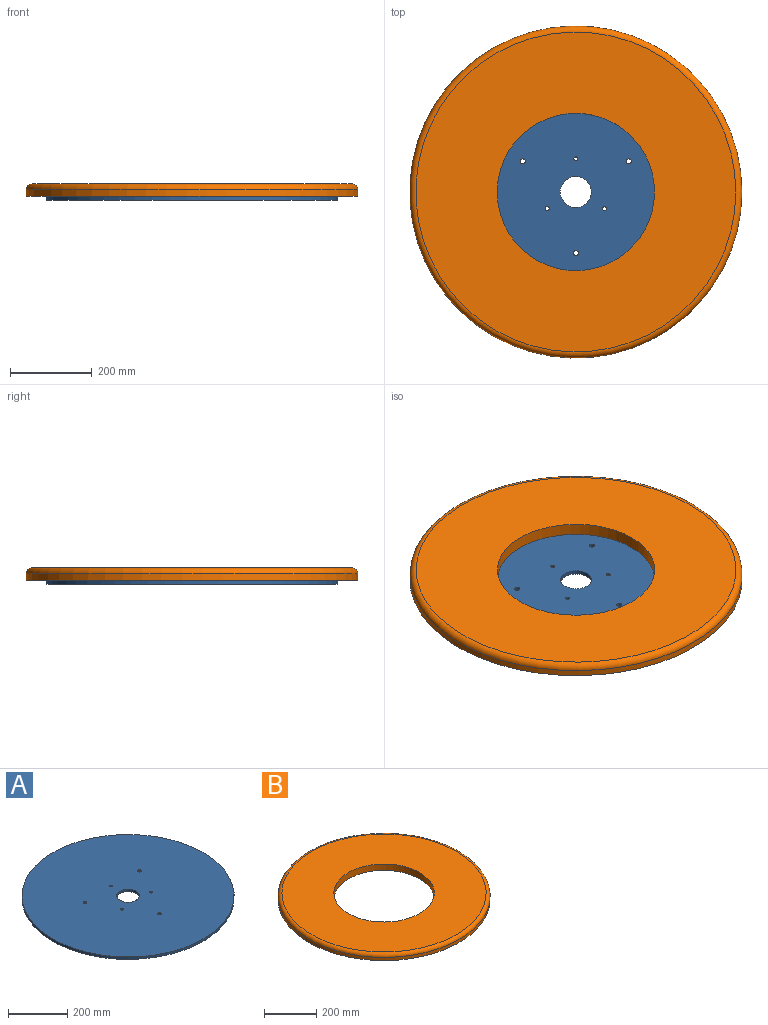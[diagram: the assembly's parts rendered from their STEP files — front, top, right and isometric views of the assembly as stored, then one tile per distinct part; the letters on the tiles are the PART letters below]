
ASSEMBLY  parts=2 mates=1
PART A: 10 faces, bbox 715x715x10 mm
  f0: cylinder r=357.5mm len=715mm, axis (0,0,-1), area 22462.4mm2, adj f1,f2
  f1: plane 715x715mm, normal (0,0,1), area 396315.1mm2, adj f0,f3,f4,f5,f6,f7,f8,f9
  f2: plane 715x715mm, normal (0,0,-1), area 396315.1mm2, adj f0,f3,f4,f5,f6,f7,f8,f9
  f3: cylinder r=38.25mm len=76.5mm, axis (0,0,-1), area 2403.3mm2, adj f1,f2
  f4: cylinder r=6.25mm len=12.5mm, axis (0,0,1), area 392.7mm2, adj f1,f2
  f5: cylinder r=6.25mm len=12.5mm, axis (0,0,1), area 392.7mm2, adj f1,f2
  f6: cylinder r=6.25mm len=12.5mm, axis (0,0,1), area 392.7mm2, adj f1,f2
  f7: cylinder r=5mm len=10mm, axis (0,0,1), area 314.2mm2, adj f1,f2
  f8: cylinder r=5mm len=10mm, axis (0,0,1), area 314.2mm2, adj f1,f2
  f9: cylinder r=5mm len=10mm, axis (0,0,1), area 314.2mm2, adj f1,f2
PART B: 5 faces, bbox 882.1x882.1x30 mm
  f0: cylinder r=407.5mm len=815mm, axis (0,0,-1), area 38406mm2, adj f2,f4
  f1: plane 785x785mm, normal (0,0,1), area 366960.8mm2, adj f3,f4
  f2: plane 815x815mm, normal (0,0,-1), area 404659.9mm2, adj f0,f3
  f3: cylinder r=193mm len=386mm, axis (0,0,-1), area 36379.6mm2, adj f1,f2
  f4: torus R=392.5mm, axis (0,0,1), area 59521mm2, adj f0,f1
PLACE A t=(-0.1,-1.77,-7.57)mm
PLACE B t=(-0.1,-1.77,2.43)mm
MATE cylindrical B.f0 <-> A.f0  axis (0,0,-1) through (-0.1,-1.77,2.43)mm
